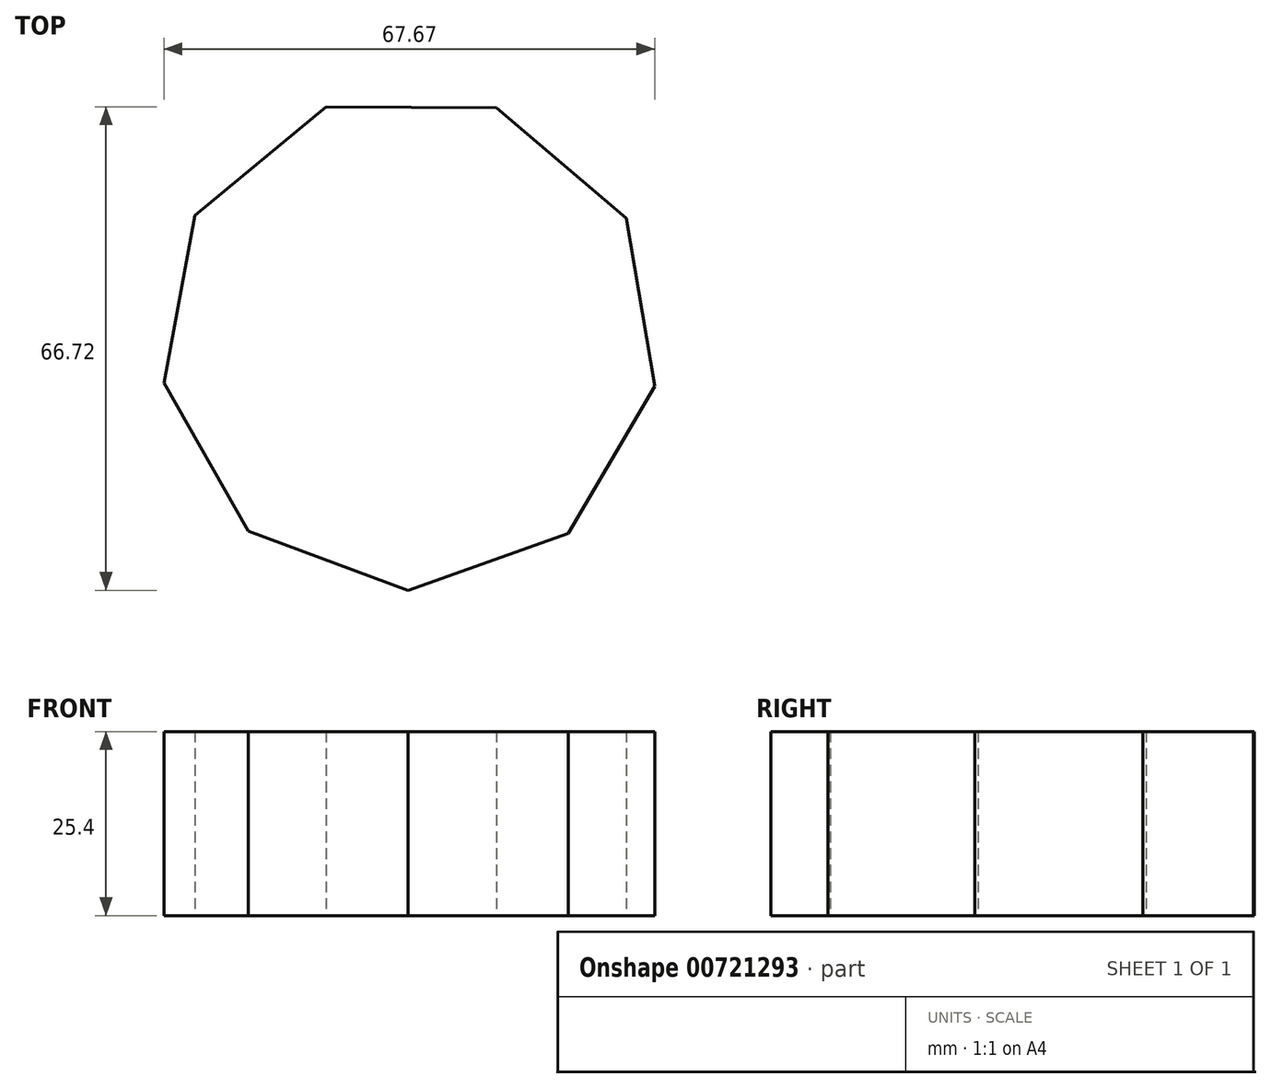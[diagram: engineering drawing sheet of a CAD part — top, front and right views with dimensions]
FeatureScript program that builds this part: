
annotation { "Feature Type Name" : "Feature", "Feature Type Description" : "" }
export const myFeature = defineFeature(function(context is Context, id is Id, definition is map)
    precondition{}
    {
        {
            var Q0;
            Q0=qCreatedBy(makeId("Top.planeOp"),FACE);
            var sketch = newSketch(context, id + "F0", { "sketchPlane" : qUnion([Q0])});
            skCircle(sketch, "E0.cCircle", {"center": v(0, -15.06) * mm, "radius": 32.28 * mm, "construction": true});
            skLineSegment(sketch, "E0.0", {"start": v(-33.88, -20.78) * mm, "end": v(-29.63, 2.33) * mm});
            skLineSegment(sketch, "E0.1", {"start": v(-29.63, 2.33) * mm, "end": v(-11.52, 17.3) * mm});
            skLineSegment(sketch, "E0.2", {"start": v(-11.52, 17.3) * mm, "end": v(11.98, 17.14) * mm});
            skLineSegment(sketch, "E0.3", {"start": v(11.98, 17.14) * mm, "end": v(29.88, 1.9) * mm});
            skLineSegment(sketch, "E0.4", {"start": v(29.88, 1.9) * mm, "end": v(33.8, -21.27) * mm});
            skLineSegment(sketch, "E0.5", {"start": v(33.8, -21.27) * mm, "end": v(21.9, -41.54) * mm});
            skLineSegment(sketch, "E0.6", {"start": v(21.9, -41.54) * mm, "end": v(-0.25, -49.41) * mm});
            skLineSegment(sketch, "E0.7", {"start": v(-0.25, -49.41) * mm, "end": v(-22.27, -41.22) * mm});
            skLineSegment(sketch, "E0.8", {"start": v(-22.27, -41.22) * mm, "end": v(-33.88, -20.78) * mm});
            skPoint(sketch, "E0.0.midPoint", {"position": v(-31.75, -9.23) * mm});
            skSolve(sketch);
        }
        {
            var Q0;
            Q0=makeQuery(id+"F0.imprint","IMPRINT",FACE,{"disambiguationData":[TD([[makeQuery(id+"F0.imprint","IMPRINT",EDGE,{"derivedFrom":sQuery(id+"F0.wireOp",EDGE,"E0.0")}),-1.0]])]});
            extrude(context, id + "F1", {"entities" : qUnion([Q0]), "depth" : 25.4 * mm, "offsetDistance" : 25.4 * mm});
        }
    });
